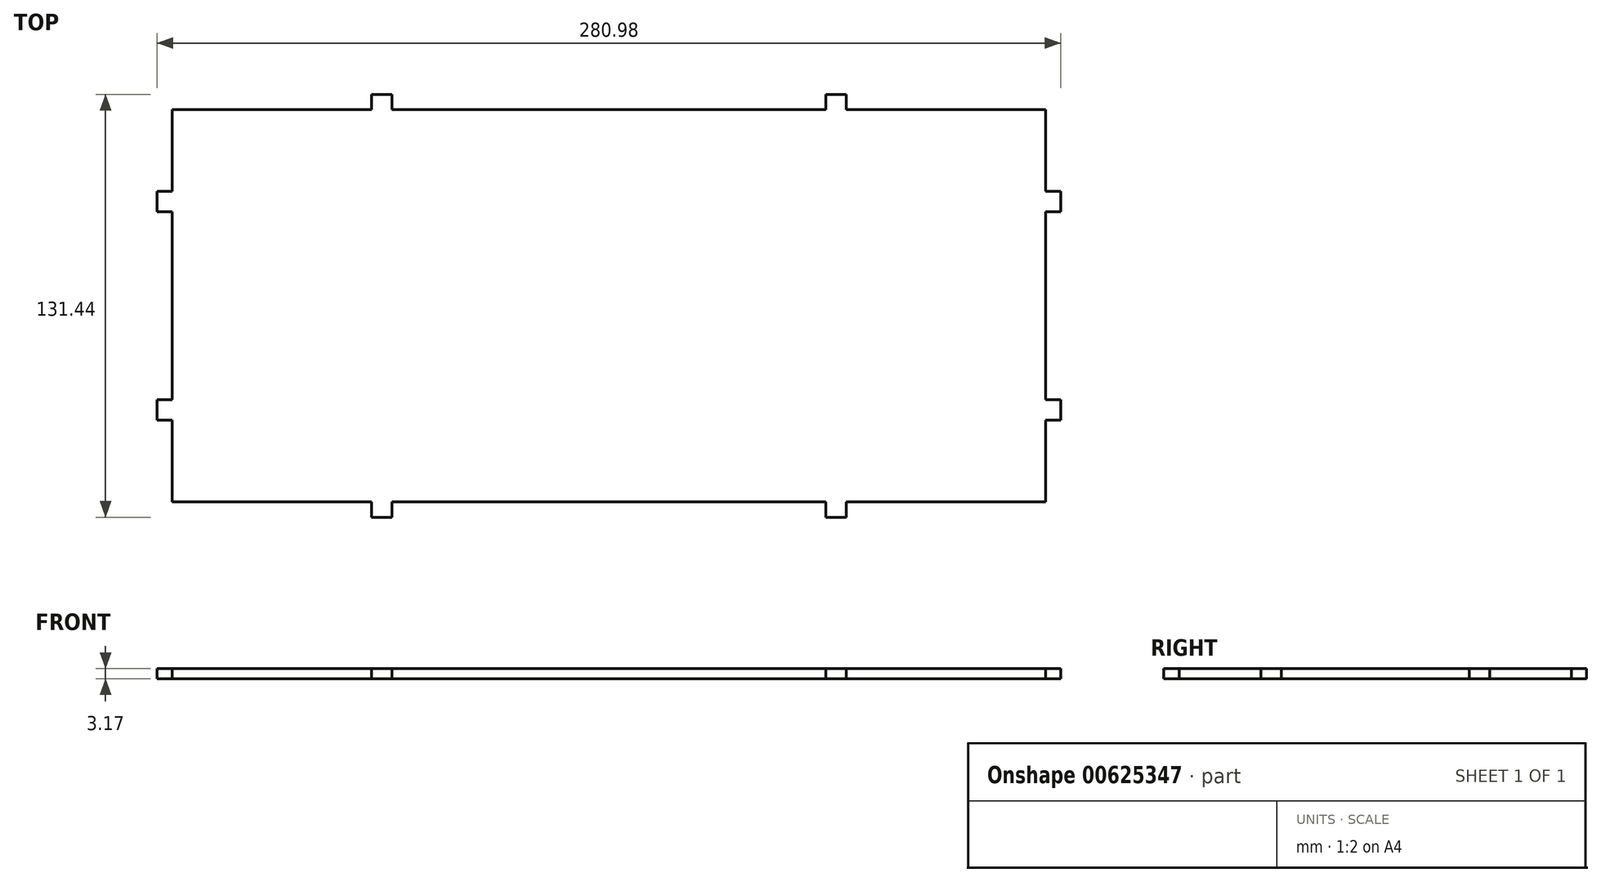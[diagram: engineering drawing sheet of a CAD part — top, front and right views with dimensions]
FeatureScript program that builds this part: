
annotation { "Feature Type Name" : "Feature", "Feature Type Description" : "" }
export const myFeature = defineFeature(function(context is Context, id is Id, definition is map)
    precondition{}
    {
        {
            var Q0;
            Q0=qCreatedBy(makeId("Top.planeOp"),FACE);
            var sketch = newSketch(context, id + "F0", { "sketchPlane" : qUnion([Q0])});
            skLineSegment(sketch, "E0.bottom", {"start": v(-135.73, 60.96) * mm, "end": v(135.73, 60.96) * mm, "construction": true});
            skLineSegment(sketch, "E0.top", {"start": v(-135.73, -60.96) * mm, "end": v(135.73, -60.96) * mm, "construction": true});
            skLineSegment(sketch, "E0.left", {"start": v(-135.73, 60.96) * mm, "end": v(-135.73, -60.96) * mm, "construction": true});
            skLineSegment(sketch, "E0.right", {"start": v(135.73, 60.96) * mm, "end": v(135.73, -60.96) * mm, "construction": true});
            skPoint(sketch, "E0.middle", {"position": v(0, 0) * mm});
            skLineSegment(sketch, "E1", {"start": v(0, 60.96) * mm, "end": v(0, 0) * mm, "construction": true});
            skLineSegment(sketch, "E2", {"start": v(-135.73, 0) * mm, "end": v(0, 0) * mm, "construction": true});
            skLineSegment(sketch, "E3", {"start": v(-73.82, 60.96) * mm, "end": v(-73.82, 65.72) * mm});
            skLineSegment(sketch, "E4", {"start": v(-73.82, 65.72) * mm, "end": v(-67.47, 65.72) * mm});
            skLineSegment(sketch, "E5", {"start": v(-67.47, 65.72) * mm, "end": v(-67.47, 60.96) * mm});
            skLineSegment(sketch, "E6", {"start": v(-67.47, 60.96) * mm, "end": v(0, 60.96) * mm});
            skLineSegment(sketch, "E7", {"start": v(-135.73, 0) * mm, "end": v(-135.73, 29.21) * mm});
            skLineSegment(sketch, "E8", {"start": v(-135.73, 29.21) * mm, "end": v(-140.5, 29.21) * mm});
            skLineSegment(sketch, "E9", {"start": v(-140.5, 29.21) * mm, "end": v(-140.5, 35.56) * mm});
            skLineSegment(sketch, "E10", {"start": v(-140.5, 35.56) * mm, "end": v(-135.73, 35.56) * mm});
            skLineSegment(sketch, "E11", {"start": v(-135.73, 35.56) * mm, "end": v(-135.73, 60.96) * mm});
            skLineSegment(sketch, "E12", {"start": v(-73.82, 60.96) * mm, "end": v(-135.73, 60.96) * mm});
            skLineSegment(sketch, "E13.MirrorCS", {"start": v(-73.82, -60.96) * mm, "end": v(-73.82, -65.72) * mm});
            skLineSegment(sketch, "E14.MirrorCS", {"start": v(-73.82, -65.72) * mm, "end": v(-67.47, -65.72) * mm});
            skLineSegment(sketch, "E15.MirrorCS", {"start": v(-67.47, -65.72) * mm, "end": v(-67.47, -60.96) * mm});
            skLineSegment(sketch, "E16.MirrorCS", {"start": v(-67.47, -60.96) * mm, "end": v(0, -60.96) * mm});
            skLineSegment(sketch, "E17.MirrorCS", {"start": v(-73.82, -60.96) * mm, "end": v(-135.73, -60.96) * mm});
            skLineSegment(sketch, "E18.MirrorCS", {"start": v(-135.73, -35.56) * mm, "end": v(-135.73, -60.96) * mm});
            skLineSegment(sketch, "E19.MirrorCS", {"start": v(-135.73, 0) * mm, "end": v(-135.73, -29.21) * mm});
            skLineSegment(sketch, "E20.MirrorCS", {"start": v(-140.5, -35.56) * mm, "end": v(-135.73, -35.56) * mm});
            skLineSegment(sketch, "E21.MirrorCS", {"start": v(-140.5, -29.21) * mm, "end": v(-140.5, -35.56) * mm});
            skLineSegment(sketch, "E22.MirrorCS", {"start": v(-135.73, -29.21) * mm, "end": v(-140.5, -29.21) * mm});
            skLineSegment(sketch, "E23.MirrorCS", {"start": v(73.82, 60.96) * mm, "end": v(73.82, 65.72) * mm});
            skLineSegment(sketch, "E24.MirrorCS", {"start": v(135.73, -29.21) * mm, "end": v(140.5, -29.21) * mm});
            skLineSegment(sketch, "E25.MirrorCS", {"start": v(140.5, -35.56) * mm, "end": v(135.73, -35.56) * mm});
            skLineSegment(sketch, "E26.MirrorCS", {"start": v(73.82, 65.72) * mm, "end": v(67.47, 65.72) * mm});
            skLineSegment(sketch, "E27.MirrorCS", {"start": v(140.5, 29.2) * mm, "end": v(140.5, 35.56) * mm});
            skLineSegment(sketch, "E28.MirrorCS", {"start": v(67.47, 65.72) * mm, "end": v(67.47, 60.96) * mm});
            skLineSegment(sketch, "E29.MirrorCS", {"start": v(140.5, 35.56) * mm, "end": v(135.73, 35.56) * mm});
            skLineSegment(sketch, "E30.MirrorCS", {"start": v(140.5, -29.21) * mm, "end": v(140.5, -35.56) * mm});
            skLineSegment(sketch, "E31.MirrorCS", {"start": v(135.73, 29.2) * mm, "end": v(140.5, 29.2) * mm});
            skLineSegment(sketch, "E32.MirrorCS", {"start": v(135.73, 0) * mm, "end": v(135.73, -29.21) * mm});
            skLineSegment(sketch, "E33.MirrorCS", {"start": v(135.73, 35.56) * mm, "end": v(135.73, 60.96) * mm});
            skLineSegment(sketch, "E34.MirrorCS", {"start": v(73.82, 60.96) * mm, "end": v(135.73, 60.96) * mm});
            skLineSegment(sketch, "E35.MirrorCS", {"start": v(135.73, 0) * mm, "end": v(135.73, 29.2) * mm});
            skLineSegment(sketch, "E36.MirrorCS", {"start": v(73.82, -60.96) * mm, "end": v(73.82, -65.72) * mm});
            skLineSegment(sketch, "E37.MirrorCS", {"start": v(67.47, -65.72) * mm, "end": v(67.47, -60.96) * mm});
            skLineSegment(sketch, "E38.MirrorCS", {"start": v(73.82, -65.72) * mm, "end": v(67.47, -65.72) * mm});
            skLineSegment(sketch, "E39.MirrorCS", {"start": v(73.82, -60.96) * mm, "end": v(135.73, -60.96) * mm});
            skLineSegment(sketch, "E40.MirrorCS", {"start": v(135.73, -35.56) * mm, "end": v(135.73, -60.96) * mm});
            skLineSegment(sketch, "E41.MirrorCS", {"start": v(67.47, -60.96) * mm, "end": v(0, -60.96) * mm});
            skLineSegment(sketch, "E42.MirrorCS", {"start": v(67.47, 60.96) * mm, "end": v(0, 60.96) * mm});
            skSolve(sketch);
        }
        {
            var Q0;
            Q0 = qSketchRegion(id + "F0", true);
            extrude(context, id + "F1", {"entities" : qUnion([Q0]), "depth" : 3.17 * mm, "offsetDistance" : 25.4 * mm});
        }
    });
